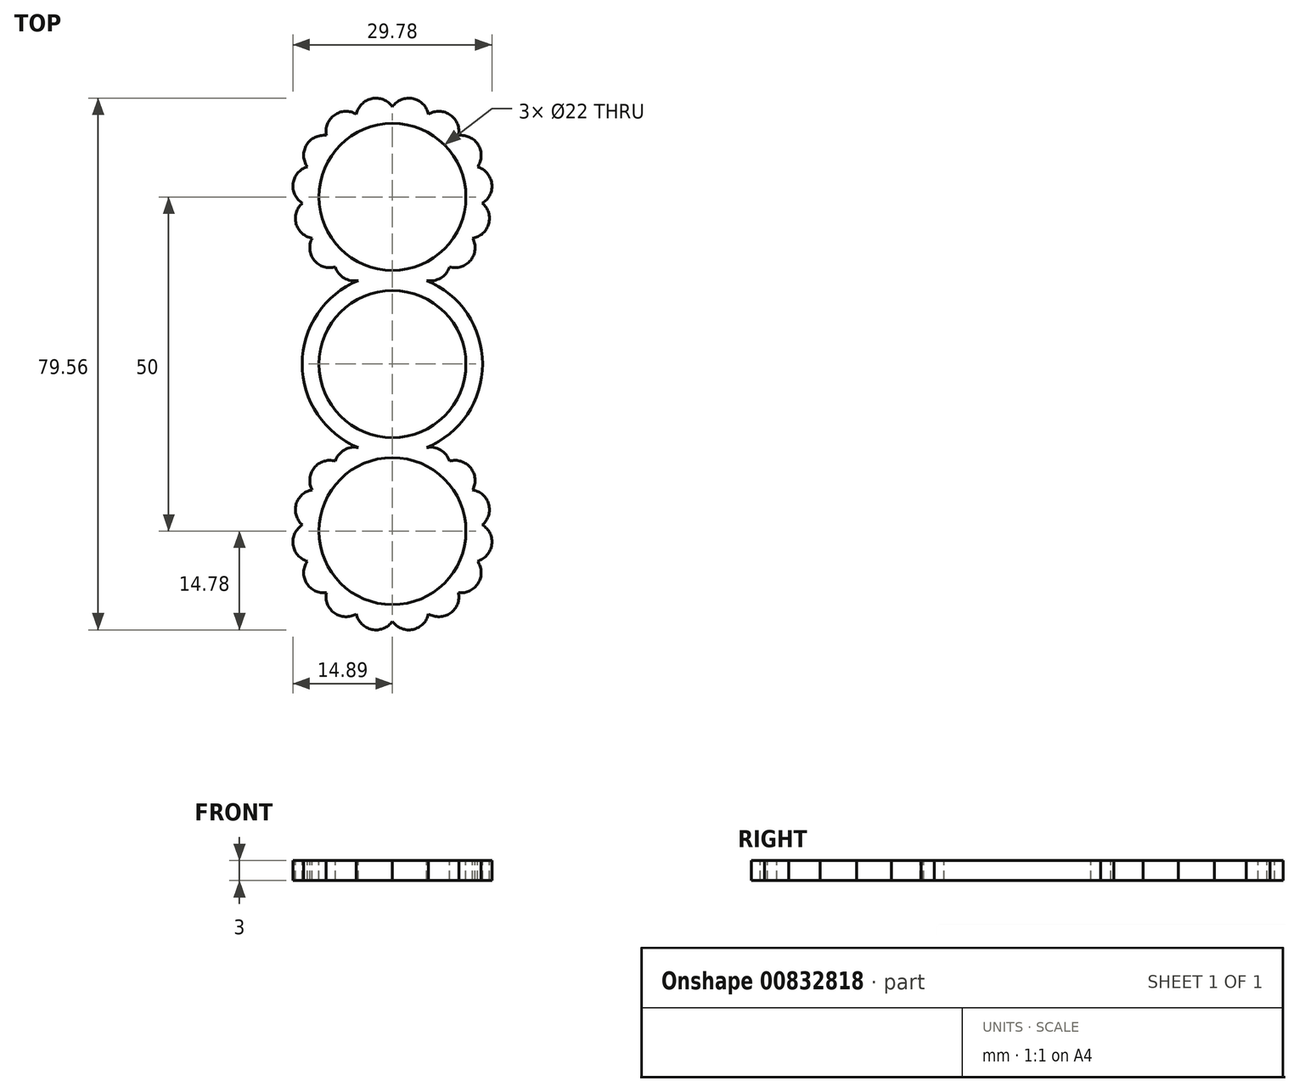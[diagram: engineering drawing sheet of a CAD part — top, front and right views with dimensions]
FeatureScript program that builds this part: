
annotation { "Feature Type Name" : "Feature", "Feature Type Description" : "" }
export const myFeature = defineFeature(function(context is Context, id is Id, definition is map)
    precondition{}
    {
        {
            var Q0;
            Q0=qCreatedBy(makeId("Top.planeOp"),FACE);
            var sketch = newSketch(context, id + "F0", { "sketchPlane" : qUnion([Q0])});
            skCircle(sketch, "E0", {"center": v(0, 0) * mm, "radius": 11 * mm});
            skArc(sketch, "E1", {"start": v(-5.1, 12.5) * mm, "mid": v(-13.5, 0) * mm, "end": v(-5.1, -12.5) * mm});
            skCircle(sketch, "E2", {"center": v(0, 25) * mm, "radius": 11 * mm});
            skCircle(sketch, "E3.MirrorC", {"center": v(0, -25) * mm, "radius": 11 * mm});
            skArc(sketch, "E4.trimOffspring", {"start": v(5.1, -12.5) * mm, "mid": v(13.5, 0) * mm, "end": v(5.1, 12.5) * mm});
            skArc(sketch, "E5", {"start": v(0, 38.5) * mm, "mid": v(-3.07, 39.71) * mm, "end": v(-5.4, 37.38) * mm});
            skArc(sketch, "E6", {"start": v(-5.4, 37.38) * mm, "mid": v(-8.68, 37.25) * mm, "end": v(-9.88, 34.2) * mm});
            skArc(sketch, "E7", {"start": v(-9.88, 34.2) * mm, "mid": v(-12.84, 32.78) * mm, "end": v(-12.73, 29.5) * mm});
            skArc(sketch, "E8", {"start": v(-12.73, 29.5) * mm, "mid": v(-14.86, 27.02) * mm, "end": v(-13.47, 24.07) * mm});
            skArc(sketch, "E9", {"start": v(-13.47, 24.07) * mm, "mid": v(-14.4, 20.98) * mm, "end": v(-12, 18.83) * mm});
            skArc(sketch, "E10", {"start": v(-12, 18.83) * mm, "mid": v(-11.7, 15.53) * mm, "end": v(-8.54, 14.52) * mm});
            skArc(sketch, "E11", {"start": v(-8.54, 14.52) * mm, "mid": v(-7.2, 12.86) * mm, "end": v(-5.1, 12.5) * mm});
            skArc(sketch, "E12.MirrorCS", {"start": v(0, 38.5) * mm, "mid": v(3.07, 39.71) * mm, "end": v(5.4, 37.38) * mm});
            skArc(sketch, "E13.MirrorCS", {"start": v(5.4, 37.38) * mm, "mid": v(8.68, 37.25) * mm, "end": v(9.88, 34.2) * mm});
            skArc(sketch, "E14.MirrorCS", {"start": v(9.88, 34.2) * mm, "mid": v(12.84, 32.78) * mm, "end": v(12.73, 29.5) * mm});
            skArc(sketch, "E15.MirrorCS", {"start": v(12.73, 29.5) * mm, "mid": v(14.86, 27.02) * mm, "end": v(13.47, 24.07) * mm});
            skArc(sketch, "E16.MirrorCS", {"start": v(13.47, 24.07) * mm, "mid": v(14.4, 20.98) * mm, "end": v(12, 18.83) * mm});
            skArc(sketch, "E17.MirrorCS", {"start": v(12, 18.83) * mm, "mid": v(11.7, 15.53) * mm, "end": v(8.54, 14.52) * mm});
            skArc(sketch, "E18.MirrorCS", {"start": v(8.54, 14.52) * mm, "mid": v(7.2, 12.86) * mm, "end": v(5.1, 12.5) * mm});
            skArc(sketch, "E19.MirrorCS", {"start": v(-8.54, -14.52) * mm, "mid": v(-7.2, -12.86) * mm, "end": v(-5.1, -12.5) * mm});
            skArc(sketch, "E20.MirrorCS", {"start": v(-12, -18.83) * mm, "mid": v(-11.7, -15.53) * mm, "end": v(-8.54, -14.52) * mm});
            skArc(sketch, "E21.MirrorCS", {"start": v(-13.47, -24.07) * mm, "mid": v(-14.4, -20.98) * mm, "end": v(-12, -18.83) * mm});
            skArc(sketch, "E22.MirrorCS", {"start": v(-12.73, -29.5) * mm, "mid": v(-14.86, -27.02) * mm, "end": v(-13.47, -24.07) * mm});
            skArc(sketch, "E23.MirrorCS", {"start": v(-9.88, -34.2) * mm, "mid": v(-12.84, -32.78) * mm, "end": v(-12.73, -29.5) * mm});
            skArc(sketch, "E24.MirrorCS", {"start": v(-5.4, -37.38) * mm, "mid": v(-8.68, -37.25) * mm, "end": v(-9.88, -34.2) * mm});
            skArc(sketch, "E25.MirrorCS", {"start": v(0, -38.5) * mm, "mid": v(-3.07, -39.71) * mm, "end": v(-5.4, -37.38) * mm});
            skArc(sketch, "E26.MirrorCS", {"start": v(0, -38.5) * mm, "mid": v(3.07, -39.71) * mm, "end": v(5.4, -37.38) * mm});
            skArc(sketch, "E27.MirrorCS", {"start": v(5.4, -37.38) * mm, "mid": v(8.68, -37.25) * mm, "end": v(9.88, -34.2) * mm});
            skArc(sketch, "E28.MirrorCS", {"start": v(9.88, -34.2) * mm, "mid": v(12.84, -32.78) * mm, "end": v(12.73, -29.5) * mm});
            skArc(sketch, "E29.MirrorCS", {"start": v(12.73, -29.5) * mm, "mid": v(14.86, -27.02) * mm, "end": v(13.47, -24.07) * mm});
            skArc(sketch, "E30.MirrorCS", {"start": v(13.47, -24.07) * mm, "mid": v(14.4, -20.98) * mm, "end": v(12, -18.83) * mm});
            skArc(sketch, "E31.MirrorCS", {"start": v(12, -18.83) * mm, "mid": v(11.7, -15.53) * mm, "end": v(8.54, -14.52) * mm});
            skArc(sketch, "E32.MirrorCS", {"start": v(8.54, -14.52) * mm, "mid": v(7.2, -12.86) * mm, "end": v(5.1, -12.5) * mm});
            skSolve(sketch);
        }
        {
            var Q0;
            Q0 = qSketchRegion(id + "F0", true);
            extrude(context, id + "F1", {"entities" : qUnion([Q0]), "oppositeDirection" : true, "depth" : 3 * mm, "offsetDistance" : 25 * mm});
        }
    });
